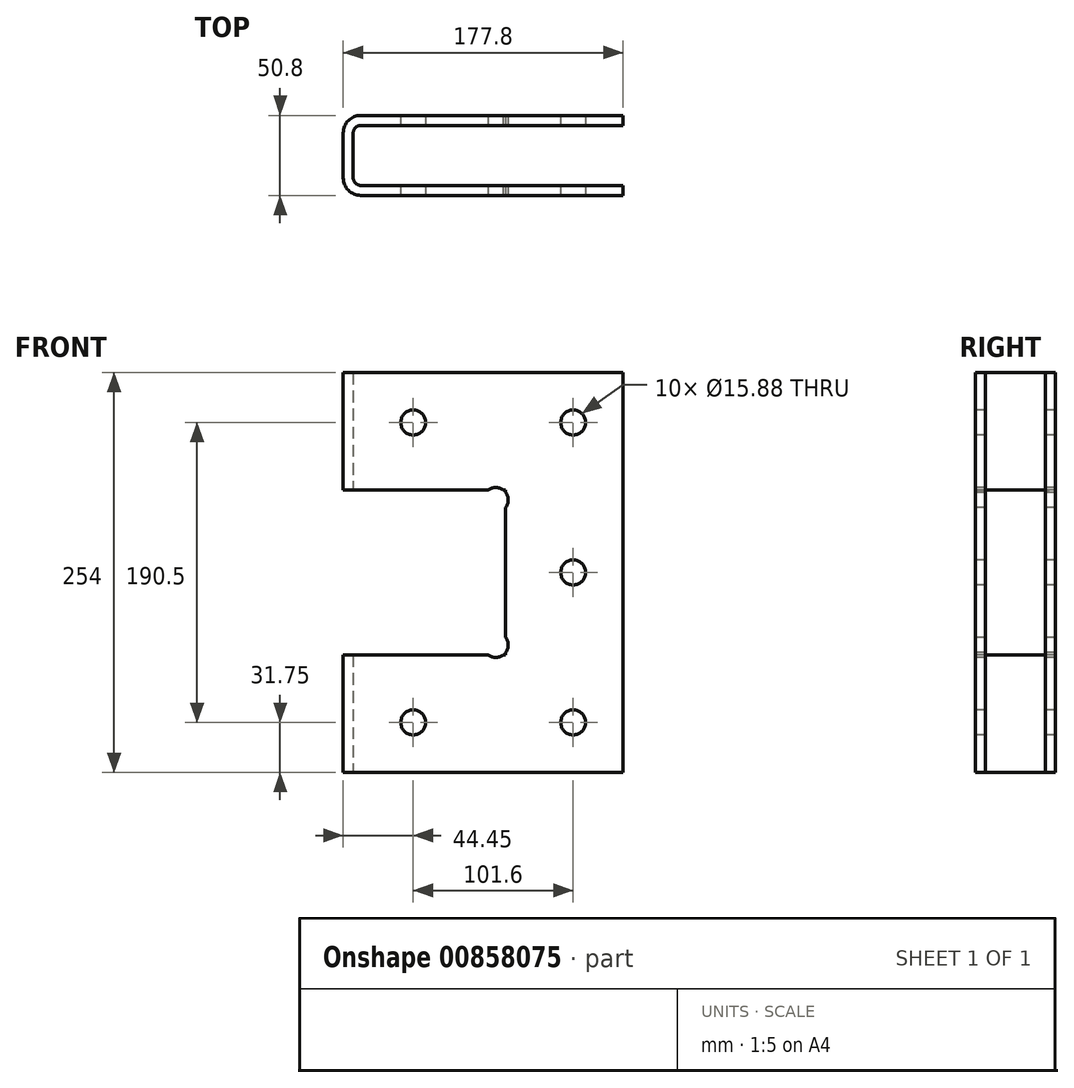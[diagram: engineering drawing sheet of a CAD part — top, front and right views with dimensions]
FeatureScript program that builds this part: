
annotation { "Feature Type Name" : "Feature", "Feature Type Description" : "" }
export const myFeature = defineFeature(function(context is Context, id is Id, definition is map)
    precondition{}
    {
        {
            var Q0;
            Q0=qCreatedBy(makeId("Top.planeOp"),FACE);
            var sketch = newSketch(context, id + "F0", { "sketchPlane" : qUnion([Q0])});
            skLineSegment(sketch, "E0.bottom", {"start": v(90.49, 25.4) * mm, "end": v(-90.49, 25.4) * mm});
            skLineSegment(sketch, "E0.top", {"start": v(90.49, -25.4) * mm, "end": v(-90.49, -25.4) * mm});
            skLineSegment(sketch, "E0.left", {"start": v(101.6, 14.29) * mm, "end": v(101.6, -14.29) * mm});
            skLineSegment(sketch, "E0.right", {"start": v(-101.6, 14.29) * mm, "end": v(-101.6, -14.29) * mm});
            skPoint(sketch, "E0.middle", {"position": v(0, 0) * mm});
            skLineSegment(sketch, "E1.0", {"start": v(90.49, 19.05) * mm, "end": v(-90.49, 19.05) * mm});
            skLineSegment(sketch, "E1.1", {"start": v(95.25, 14.29) * mm, "end": v(95.25, -14.29) * mm});
            skLineSegment(sketch, "E1.2", {"start": v(90.49, -19.05) * mm, "end": v(-90.49, -19.05) * mm});
            skLineSegment(sketch, "E1.3", {"start": v(-95.25, 14.29) * mm, "end": v(-95.25, -14.29) * mm});
            skPoint(sketch, "E2.visualSharp", {"position": v(-95.25, 19.05) * mm});
            skArc(sketch, "E2.filletArc", {"start": v(-90.49, 19.05) * mm, "mid": v(-93.86, 17.66) * mm, "end": v(-95.25, 14.29) * mm});
            skPoint(sketch, "E3.visualSharp", {"position": v(-95.25, -19.05) * mm});
            skArc(sketch, "E3.filletArc", {"start": v(-95.25, -14.29) * mm, "mid": v(-93.86, -17.66) * mm, "end": v(-90.49, -19.05) * mm});
            skPoint(sketch, "E4.visualSharp", {"position": v(95.25, 19.05) * mm});
            skArc(sketch, "E4.filletArc", {"start": v(95.25, 14.29) * mm, "mid": v(93.86, 17.66) * mm, "end": v(90.49, 19.05) * mm});
            skPoint(sketch, "E5.visualSharp", {"position": v(95.25, -19.05) * mm});
            skArc(sketch, "E5.filletArc", {"start": v(90.49, -19.05) * mm, "mid": v(93.86, -17.66) * mm, "end": v(95.25, -14.29) * mm});
            skArc(sketch, "E6.0", {"start": v(-90.49, 25.4) * mm, "mid": v(-98.35, 22.15) * mm, "end": v(-101.6, 14.29) * mm});
            skArc(sketch, "E7.0", {"start": v(-101.6, -14.29) * mm, "mid": v(-98.35, -22.15) * mm, "end": v(-90.49, -25.4) * mm});
            skArc(sketch, "E8.0", {"start": v(90.49, -25.4) * mm, "mid": v(98.35, -22.15) * mm, "end": v(101.6, -14.29) * mm});
            skArc(sketch, "E9.0", {"start": v(101.6, 14.29) * mm, "mid": v(98.35, 22.15) * mm, "end": v(90.49, 25.4) * mm});
            skPoint(sketch, "E10.orphan", {"position": v(-101.6, 25.4) * mm});
            skPoint(sketch, "E11.orphan", {"position": v(101.6, 25.4) * mm});
            skPoint(sketch, "E12.orphan", {"position": v(101.6, -25.4) * mm});
            skPoint(sketch, "E13.orphan", {"position": v(-101.6, -25.4) * mm});
            skSolve(sketch);
        }
        {
            var Q0;
            Q0 = qSketchRegion(id + "F0", true);
            extrude(context, id + "F1", {"entities" : qUnion([Q0]), "depth" : 254 * mm, "offsetDistance" : 25.4 * mm});
        }
        {
            var Q0;
            Q0=makeQuery(id+"F1.opExtrude","CAP_FACE",FACE,{"disambiguationData":[OSD([sQuery(id+"F0.wireOp",EDGE,"E0.bottom"),sQuery(id+"F0.wireOp",EDGE,"E0.top"),sQuery(id+"F0.wireOp",EDGE,"E0.left"),sQuery(id+"F0.wireOp",EDGE,"E0.right"),sQuery(id+"F0.wireOp",EDGE,"E1.0"),sQuery(id+"F0.wireOp",EDGE,"E1.1"),sQuery(id+"F0.wireOp",EDGE,"E1.2"),sQuery(id+"F0.wireOp",EDGE,"E1.3"),sQuery(id+"F0.wireOp",EDGE,"E2.filletArc"),sQuery(id+"F0.wireOp",EDGE,"E3.filletArc"),sQuery(id+"F0.wireOp",EDGE,"E4.filletArc"),sQuery(id+"F0.wireOp",EDGE,"E5.filletArc"),sQuery(id+"F0.wireOp",EDGE,"E6.0"),sQuery(id+"F0.wireOp",EDGE,"E7.0"),sQuery(id+"F0.wireOp",EDGE,"E8.0"),sQuery(id+"F0.wireOp",EDGE,"E9.0")])],"isStart":false});
            var sketch = newSketch(context, id + "F2", { "sketchPlane" : qUnion([Q0])});
            skLineSegment(sketch, "E14.0", {"start": v(-101.6, 14.29) * mm, "end": v(-101.6, -14.29) * mm});
            skLineSegment(sketch, "E15.0", {"start": v(76.2, 14.29) * mm, "end": v(76.2, -14.29) * mm});
            skLineSegment(sketch, "E16", {"start": v(76.2, 0) * mm, "end": v(76.2, 25.4) * mm});
            skLineSegment(sketch, "E17", {"start": v(76.2, 25.4) * mm, "end": v(101.6, 25.4) * mm});
            skLineSegment(sketch, "E18", {"start": v(101.6, 25.4) * mm, "end": v(101.6, -25.4) * mm});
            skLineSegment(sketch, "E19", {"start": v(101.6, -25.4) * mm, "end": v(76.2, -25.4) * mm});
            skLineSegment(sketch, "E20", {"start": v(76.2, -25.4) * mm, "end": v(76.2, 0) * mm});
            skSolve(sketch);
        }
        {
            var Q0;
            Q0 = qSketchRegion(id + "F2", true);
            extrude(context, id + "F3", {"entities" : qUnion([Q0]), "operationType" : NewBodyOperationType.REMOVE, "oppositeDirection" : true, "depth" : 278.9 * mm, "offsetDistance" : 25.4 * mm});
        }
        {
            var Q0;
            Q0=makeQuery(id+"F1.opExtrude","SWEPT_FACE",FACE,{"disambiguationData":[OSD([sQuery(id+"F0.wireOp",EDGE,"E0.top")])]});
            var sketch = newSketch(context, id + "F4", { "sketchPlane" : qUnion([Q0])});
            skLineSegment(sketch, "E21.0", {"start": v(-101.6, 254) * mm, "end": v(-101.6, 0) * mm});
            skLineSegment(sketch, "E22", {"start": v(-101.6, 127) * mm, "end": v(-101.6, 179.4) * mm});
            skLineSegment(sketch, "E23", {"start": v(-101.6, 179.4) * mm, "end": v(1.6, 179.4) * mm});
            skLineSegment(sketch, "E24", {"start": v(1.6, 179.4) * mm, "end": v(1.6, 74.63) * mm});
            skLineSegment(sketch, "E25", {"start": v(1.6, 74.63) * mm, "end": v(-101.6, 74.63) * mm});
            skLineSegment(sketch, "E26", {"start": v(-101.6, 74.63) * mm, "end": v(-101.6, 127) * mm});
            skSolve(sketch);
        }
        {
            var Q0;
            Q0 = qSketchRegion(id + "F4", true);
            extrude(context, id + "F5", {"entities" : qUnion([Q0]), "operationType" : NewBodyOperationType.REMOVE, "oppositeDirection" : true, "depth" : 122.94 * mm, "offsetDistance" : 25.4 * mm});
        }
        {
            var Q0;
            Q0=makeQuery(id+"F1.opExtrude","SWEPT_FACE",FACE,{"disambiguationData":[OSD([sQuery(id+"F0.wireOp",EDGE,"E0.top")])]});
            var sketch = newSketch(context, id + "F6", { "sketchPlane" : qUnion([Q0])});
            skLineSegment(sketch, "E27.0", {"start": v(44.45, 222.25) * mm, "end": v(-90.49, 222.25) * mm});
            skLineSegment(sketch, "E27.1", {"start": v(44.45, 31.75) * mm, "end": v(44.45, 222.25) * mm});
            skLineSegment(sketch, "E27.2", {"start": v(44.45, 31.75) * mm, "end": v(-90.49, 31.75) * mm});
            skLineSegment(sketch, "E28.0", {"start": v(-101.6, 254) * mm, "end": v(-101.6, 179.4) * mm});
            skLineSegment(sketch, "E29.0", {"start": v(-101.6, 74.63) * mm, "end": v(-101.6, 0) * mm});
            skLineSegment(sketch, "E30.0", {"start": v(-57.15, 254) * mm, "end": v(-57.15, 179.4) * mm});
            skLineSegment(sketch, "E31.0", {"start": v(-57.15, 74.63) * mm, "end": v(-57.15, 0) * mm});
            skLineSegment(sketch, "E32", {"start": v(76.2, 127) * mm, "end": v(0, 127) * mm});
            skCircle(sketch, "E33", {"center": v(44.45, 222.25) * mm, "radius": 7.94 * mm});
            skCircle(sketch, "E34", {"center": v(44.45, 31.75) * mm, "radius": 7.94 * mm});
            skCircle(sketch, "E35", {"center": v(-57.15, 31.75) * mm, "radius": 7.94 * mm});
            skCircle(sketch, "E36", {"center": v(-57.15, 222.25) * mm, "radius": 7.94 * mm});
            skCircle(sketch, "E37", {"center": v(44.45, 127) * mm, "radius": 7.94 * mm});
            skLineSegment(sketch, "E38.0", {"start": v(-4.75, 80.98) * mm, "end": v(-90.49, 80.98) * mm, "construction": true});
            skLineSegment(sketch, "E38.1", {"start": v(-4.75, 173.05) * mm, "end": v(-4.75, 80.98) * mm, "construction": true});
            skLineSegment(sketch, "E38.2", {"start": v(-90.49, 173.05) * mm, "end": v(-4.75, 173.05) * mm, "construction": true});
            skCircle(sketch, "E39", {"center": v(-4.75, 173.05) * mm, "radius": 7.94 * mm});
            skCircle(sketch, "E40", {"center": v(-4.75, 80.98) * mm, "radius": 7.94 * mm});
            skSolve(sketch);
        }
        {
            var Q0;
            Q0 = qSketchRegion(id + "F6", true);
            extrude(context, id + "F7", {"entities" : qUnion([Q0]), "operationType" : NewBodyOperationType.REMOVE, "oppositeDirection" : true, "depth" : 101.35 * mm, "offsetDistance" : 25.4 * mm});
        }
    });
